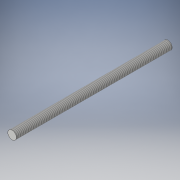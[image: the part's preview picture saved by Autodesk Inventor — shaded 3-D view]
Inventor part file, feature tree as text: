
AUTODESK INVENTOR PART (.ipt)
format: ipt  version: 2017 (Build 210142000, 142)  size: 94,720 bytes
history: native  units: in
note: dims shown in document units (in); Inventor stores cm internally (conversion verified against a paired STEP export)
features: extrude x1, thread x1, sketch x1
ambient origin geometry x8: Origin, YZ Plane, XZ Plane, XY Plane, X Axis, Y Axis, Z Axis, Center Point
bodies: Solid1 (feature_tree)
feature tree (3):
  extrude  "Extrusion1"  Depth=3.0in TaperAngle=0.0deg
  thread  "Thread1"  [1 undecoded]
  sketch  "Sketch1"  dims[d0=0.164in d1=3.0in d2=0.0in d3=1.0in d4=0.0in]
note: 1 required parameter value undecoded (feature->parameter linkage not recoverable at this tier; creation-order binding heuristic only, values carry confidence <= 0.55)
